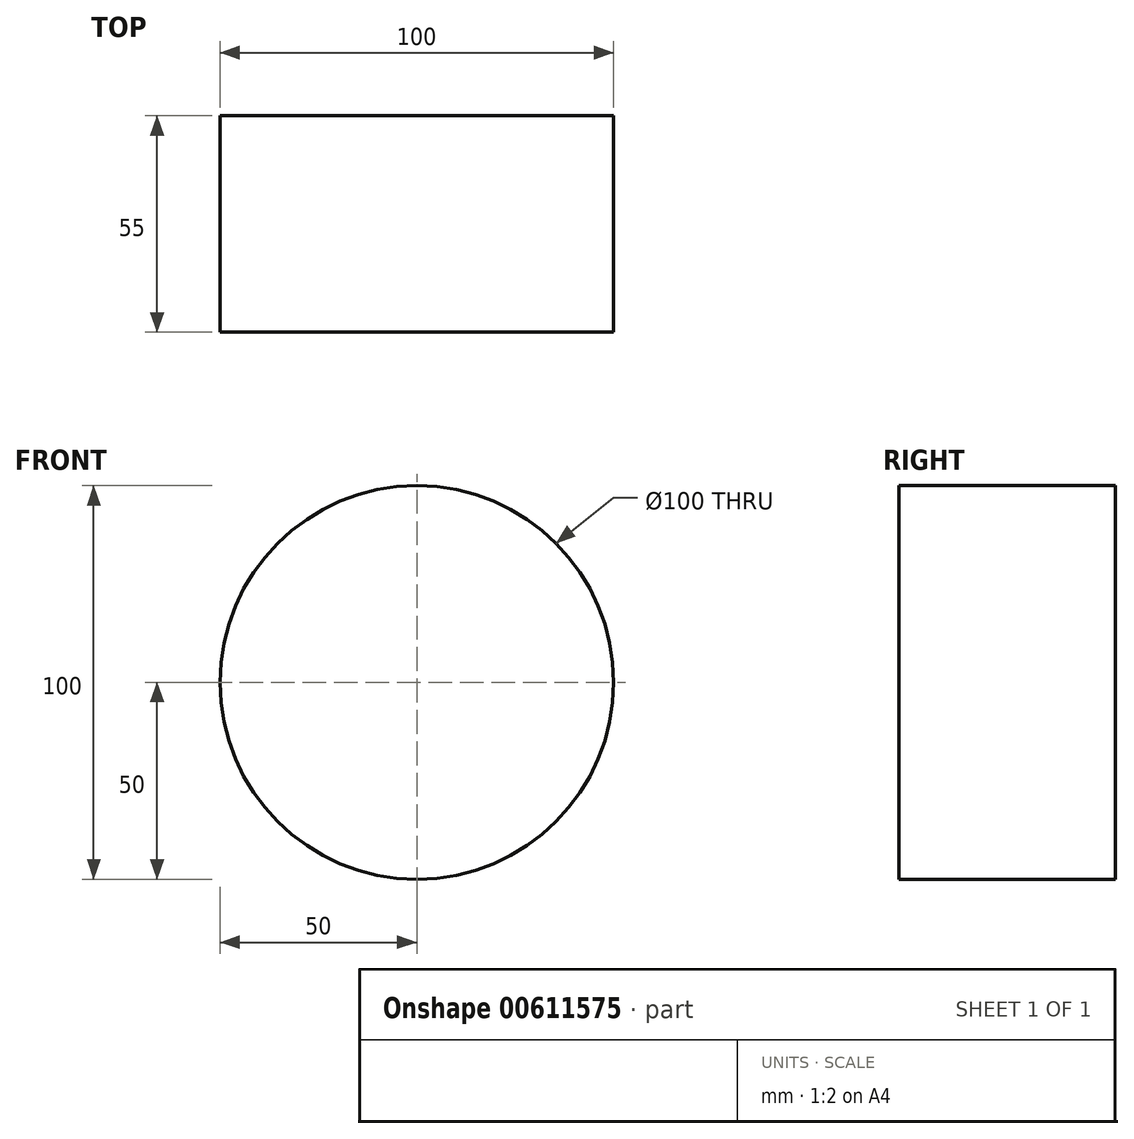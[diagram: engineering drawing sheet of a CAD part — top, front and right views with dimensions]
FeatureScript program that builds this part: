
annotation { "Feature Type Name" : "Feature", "Feature Type Description" : "" }
export const myFeature = defineFeature(function(context is Context, id is Id, definition is map)
    precondition{}
    {
        {
            var Q0;
            Q0=qCreatedBy(makeId("Front.planeOp"),FACE);
            var sketch = newSketch(context, id + "F0", { "sketchPlane" : qUnion([Q0])});
            skCircle(sketch, "E0", {"center": v(0, 0) * mm, "radius": 50 * mm});
            skSolve(sketch);
        }
        {
            var Q0;
            Q0=makeQuery(id+"F0.imprint","IMPRINT",FACE,{"disambiguationData":[TD([[makeQuery(id+"F0.imprint","IMPRINT",EDGE,{"derivedFrom":sQuery(id+"F0.wireOp",EDGE,"E0")}),1.0]])]});
            var Q1;
            Q1=sQuery(id+"F0.wireOp",EDGE,"E0");
            extrude(context, id + "F1", {"entities" : qUnion([Q0]), "bodyType" : ToolBodyType.SURFACE, "surfaceEntities" : qUnion([Q1]), "oppositeDirection" : true, "depth" : 55 * mm, "offsetDistance" : 25 * mm});
        }
    });
